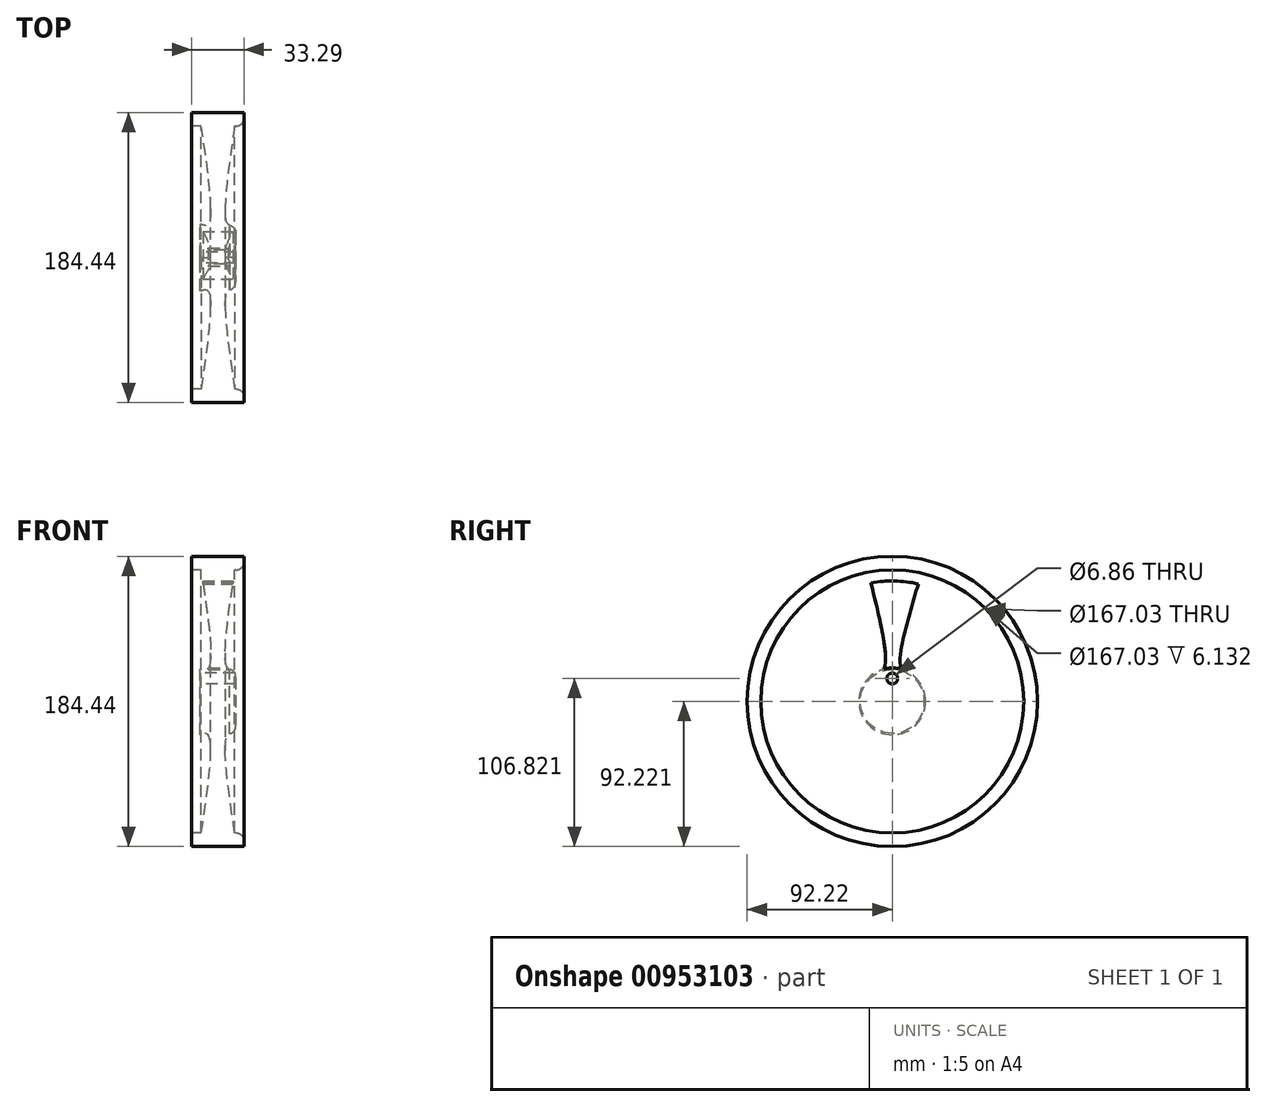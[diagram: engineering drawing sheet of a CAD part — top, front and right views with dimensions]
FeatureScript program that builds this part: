
annotation { "Feature Type Name" : "Feature", "Feature Type Description" : "" }
export const myFeature = defineFeature(function(context is Context, id is Id, definition is map)
    precondition{}
    {
        {
            var Q0;
            Q0=qCreatedBy(makeId("Front.planeOp"),FACE);
            var sketch = newSketch(context, id + "F0", { "sketchPlane" : qUnion([Q0])});
            skLineSegment(sketch, "E0", {"start": v(-52.05, 41.19) * mm, "end": v(-30.85, 41.19) * mm});
            skPoint(sketch, "E1.startSnap0", {"position": v(-41.45, 41.19) * mm});
            skLineSegment(sketch, "E2.top", {"start": v(-30.13, -42.33) * mm, "end": v(-52.77, -42.33) * mm});
            skLineSegment(sketch, "E2.left", {"start": v(-30.13, -21.15) * mm, "end": v(-30.13, -42.33) * mm});
            skPoint(sketch, "E2.middle", {"position": v(-41.45, -31.74) * mm});
            skPoint(sketch, "E3.orphan", {"position": v(-41.45, -21.15) * mm});
            skFitSpline(sketch, "E4", {"points": [v(-52.05, 41.19) * mm, v(-47.8, -21.15) * mm, v(-52.77, -21.15) * mm], "startDerivative": vector(16.39, -111.09) * mm, "endDerivative": vector(-25.68, 8.8) * mm});
            skFitSpline(sketch, "E5", {"points": [v(-30.85, 41.19) * mm, v(-35.1, -21.15) * mm, v(-30.13, -21.15) * mm], "startDerivative": vector(-16.39, -111.09) * mm, "endDerivative": vector(25.68, 8.8) * mm});
            skLineSegment(sketch, "E6", {"start": v(-52.77, -21.15) * mm, "end": v(-52.77, -42.33) * mm});
            skSolve(sketch);
        }
        {
            var Q0;
            Q0=makeQuery(id+"F0.imprint","IMPRINT",FACE,{"disambiguationData":[TD([[makeQuery(id+"F0.imprint","IMPRINT",EDGE,{"derivedFrom":sQuery(id+"F0.wireOp",EDGE,"E0")}),-1.0]])]});
            var Q1;
            Q1=sQuery(id+"F0.wireOp",EDGE,"E2.top");
            revolve(context, id + "F1", {"surfaceOperationType" : NewSurfaceOperationType.NEW, "entities" : qUnion([Q0]), "axis" : qUnion([Q1]), "revolveType" : RevolveType.FULL});
        }
        {
            var Q0;
            Q0=makeQuery(id+"F1.opRevolve","SWEPT_FACE",FACE,{"disambiguationData":[OSD([sQuery(id+"F0.wireOp",EDGE,"E2.left")])]});
            var sketch = newSketch(context, id + "F2", { "sketchPlane" : qUnion([Q0])});
            skArc(sketch, "E7", {"start": v(5.9, -21.95) * mm, "mid": v(0.29, -21.12) * mm, "end": v(-5.35, -21.8) * mm});
            skArc(sketch, "E8", {"start": v(16.5, 32.36) * mm, "mid": v(1.47, 34.15) * mm, "end": v(-13.61, 32.94) * mm});
            skFitSpline(sketch, "E9", {"points": [v(-13.61, 32.94) * mm, v(-5.35, -21.8) * mm, v(-11.46, -24.52) * mm], "startDerivative": vector(24.06, -97.23) * mm, "endDerivative": vector(-28.19, -2.4) * mm});
            skFitSpline(sketch, "E10", {"points": [v(16.5, 32.36) * mm, v(5.9, -21.95) * mm, v(11.53, -24.52) * mm], "startDerivative": vector(-27.87, -95.79) * mm, "endDerivative": vector(22.32, -6.16) * mm});
            skSolve(sketch);
        }
        {
            var Q0;
            Q0=makeQuery(id+"F2.imprint","IMPRINT",FACE,{"disambiguationData":[TD([[makeQuery(id+"F2.imprint","IMPRINT",EDGE,{"derivedFrom":sQuery(id+"F2.wireOp",EDGE,"E7")}),-1.0]])]});
            var Q1;
            Q1=makeQuery(id+"F1.opRevolve","SWEPT_FACE",FACE,{"disambiguationData":[OSD([sQuery(id+"F0.wireOp",EDGE,"E4")])]});
            extrude(context, id + "F3", {"entities" : qUnion([Q0]), "operationType" : NewBodyOperationType.REMOVE, "endBound" : BoundingType.UP_TO_SURFACE, "oppositeDirection" : true, "depth" : 25.4 * mm, "endBoundEntityFace" : qUnion([Q1]), "offsetDistance" : 25.4 * mm});
        }
        {
            var Q0;
            Q0=makeQuery(id+"F1.opRevolve","SWEPT_FACE",FACE,{"disambiguationData":[OSD([sQuery(id+"F0.wireOp",EDGE,"E6")])]});
            var sketch = newSketch(context, id + "F4", { "sketchPlane" : qUnion([Q0])});
            skCircle(sketch, "E11", {"center": v(0, -27.73) * mm, "radius": 3.43 * mm});
            skSolve(sketch);
        }
        {
            var Q0;
            Q0 = qSketchRegion(id + "F4", true);
            extrude(context, id + "F5", {"entities" : qUnion([Q0]), "operationType" : NewBodyOperationType.REMOVE, "oppositeDirection" : true, "depth" : 25.4 * mm, "offsetDistance" : 25.4 * mm});
        }
        {
            var Q0;
            Q0=qCreatedBy(makeId("Front.planeOp"),FACE);
            var sketch = newSketch(context, id + "F6", { "sketchPlane" : qUnion([Q0])});
            skLineSegment(sketch, "E12", {"start": v(-30.85, -125.84) * mm, "end": v(-52.05, -125.84) * mm});
            skLineSegment(sketch, "E13", {"start": v(-52.05, 41.19) * mm, "end": v(-30.85, 41.19) * mm});
            skLineSegment(sketch, "E14.bottom", {"start": v(-24.9, 41.19) * mm, "end": v(-58.19, 41.19) * mm});
            skLineSegment(sketch, "E14.top", {"start": v(-24.9, 49.89) * mm, "end": v(-58.19, 49.89) * mm});
            skLineSegment(sketch, "E14.left", {"start": v(-24.9, 41.19) * mm, "end": v(-24.9, 49.89) * mm});
            skLineSegment(sketch, "E14.right", {"start": v(-58.19, 41.19) * mm, "end": v(-58.19, 49.89) * mm});
            skSolve(sketch);
        }
        {
            var Q0;
            Q0=makeQuery(id+"F6.imprint","IMPRINT",FACE,{"disambiguationData":[TD([[makeQuery(id+"F6.imprint","IMPRINT",EDGE,{"derivedFrom":sQuery(id+"F6.wireOp",EDGE,"E14.top")}),1.0]])]});
            var Q1;
            Q1=makeQuery(id+"F1.opRevolve","SWEPT_FACE",FACE,{"disambiguationData":[OSD([sQuery(id+"F0.wireOp",EDGE,"E0")])]});
            revolve(context, id + "F7", {"operationType" : NewBodyOperationType.ADD, "surfaceOperationType" : NewSurfaceOperationType.NEW, "entities" : qUnion([Q0]), "axis" : qUnion([Q1]), "revolveType" : RevolveType.FULL});
        }
        {
            var Q0;
            Q0=makeQuery(id+"F7.opRevolve","SWEPT_EDGE",EDGE,{"disambiguationData":[OSD([sQuery(id+"F6.wireOp",EDGE,"E14.bottom"),sQuery(id+"F6.wireOp",EDGE,"E14.left")])]});
            var Q1;
            Q1=makeQuery(id+"F1.opRevolve","SWEPT_EDGE",EDGE,{"disambiguationData":[OSD([sQuery(id+"F0.wireOp",EDGE,"E2.left"),sQuery(id+"F0.wireOp",EDGE,"E5")])]});
            fillet(context, id + "F8", {"entities" : qUnion([Q0, Q1]), "radius" : 5.08 * mm, "tangentPropagation" : true, "allowEdgeOverflow" : false});
        }
    });
